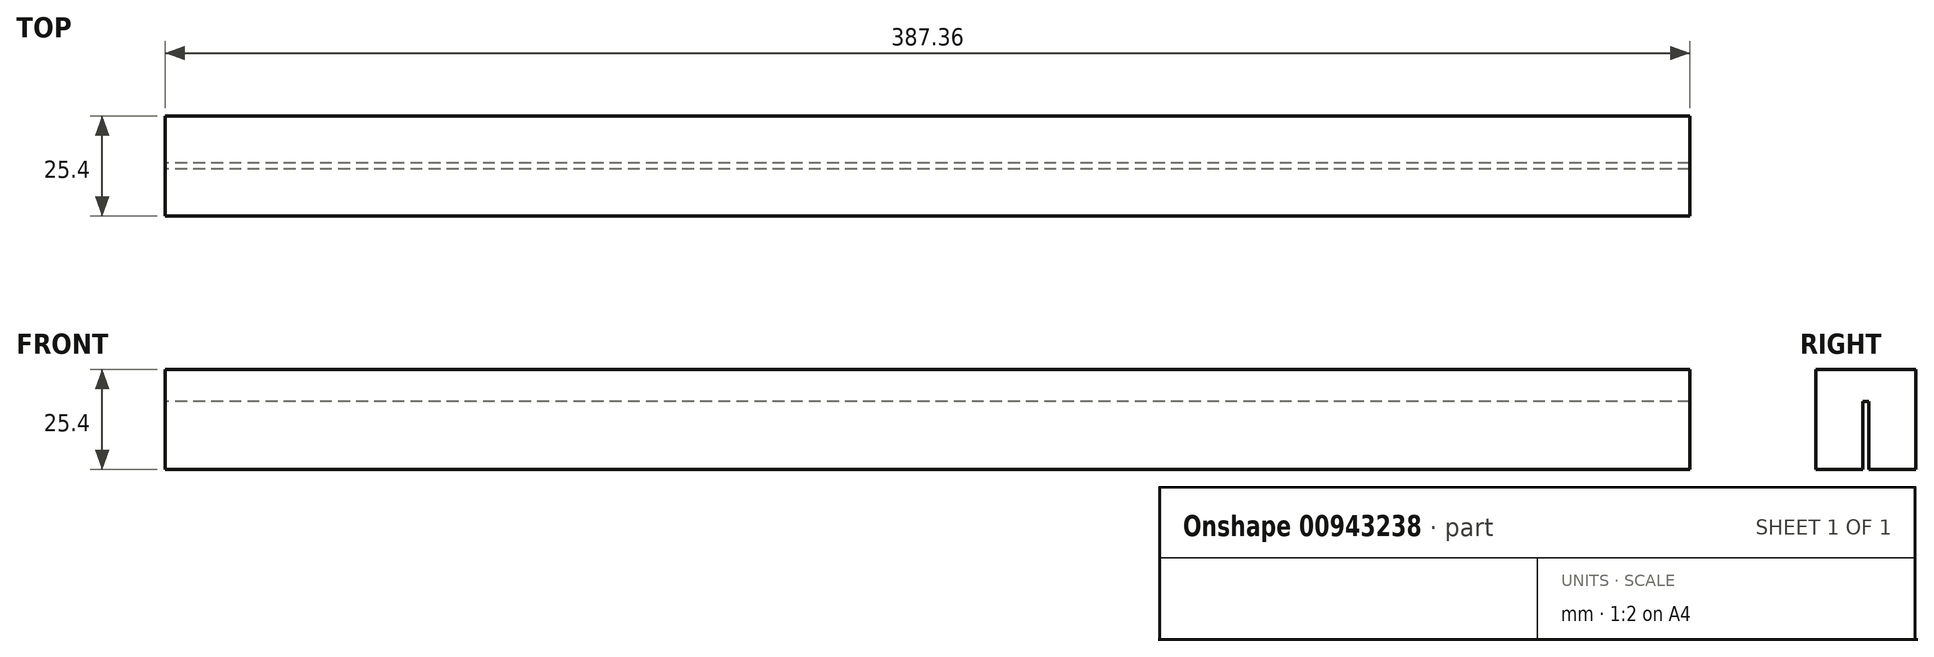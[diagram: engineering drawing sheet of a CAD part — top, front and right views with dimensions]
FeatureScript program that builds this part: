
annotation { "Feature Type Name" : "Feature", "Feature Type Description" : "" }
export const myFeature = defineFeature(function(context is Context, id is Id, definition is map)
    precondition{}
    {
        {
            var Q0;
            Q0=qCreatedBy(makeId("Right.planeOp"),FACE);
            var sketch = newSketch(context, id + "F0", { "sketchPlane" : qUnion([Q0])});
            skLineSegment(sketch, "E0.bottom", {"start": v(-12.7, 12.7) * mm, "end": v(12.7, 12.7) * mm});
            skLineSegment(sketch, "E0.top", {"start": v(-12.7, -12.7) * mm, "end": v(-0.8, -12.7) * mm});
            skLineSegment(sketch, "E0.left", {"start": v(-12.7, 12.7) * mm, "end": v(-12.7, -12.7) * mm});
            skLineSegment(sketch, "E0.right", {"start": v(12.7, 12.7) * mm, "end": v(12.7, -12.7) * mm});
            skLineSegment(sketch, "E1", {"start": v(-12.7, -12.7) * mm, "end": v(12.7, 12.7) * mm, "construction": true});
            skLineSegment(sketch, "E2.top", {"start": v(-0.8, 4.57) * mm, "end": v(0.8, 4.57) * mm});
            skLineSegment(sketch, "E2.left", {"start": v(-0.8, -12.7) * mm, "end": v(-0.8, 4.57) * mm});
            skLineSegment(sketch, "E2.right", {"start": v(0.8, -12.7) * mm, "end": v(0.8, 4.57) * mm});
            skLineSegment(sketch, "E3", {"start": v(0, 0) * mm, "end": v(0, 4.57) * mm, "construction": true});
            skLineSegment(sketch, "E4.trimOffspring", {"start": v(0.8, -12.7) * mm, "end": v(12.7, -12.7) * mm});
            skSolve(sketch);
        }
        {
            var Q0;
            Q0 = qSketchRegion(id + "F0", true);
            extrude(context, id + "F1", {"entities" : qUnion([Q0]), "endBound" : BoundingType.SYMMETRIC, "depth" : 387.35 * mm, "offsetDistance" : 25.4 * mm});
        }
    });
